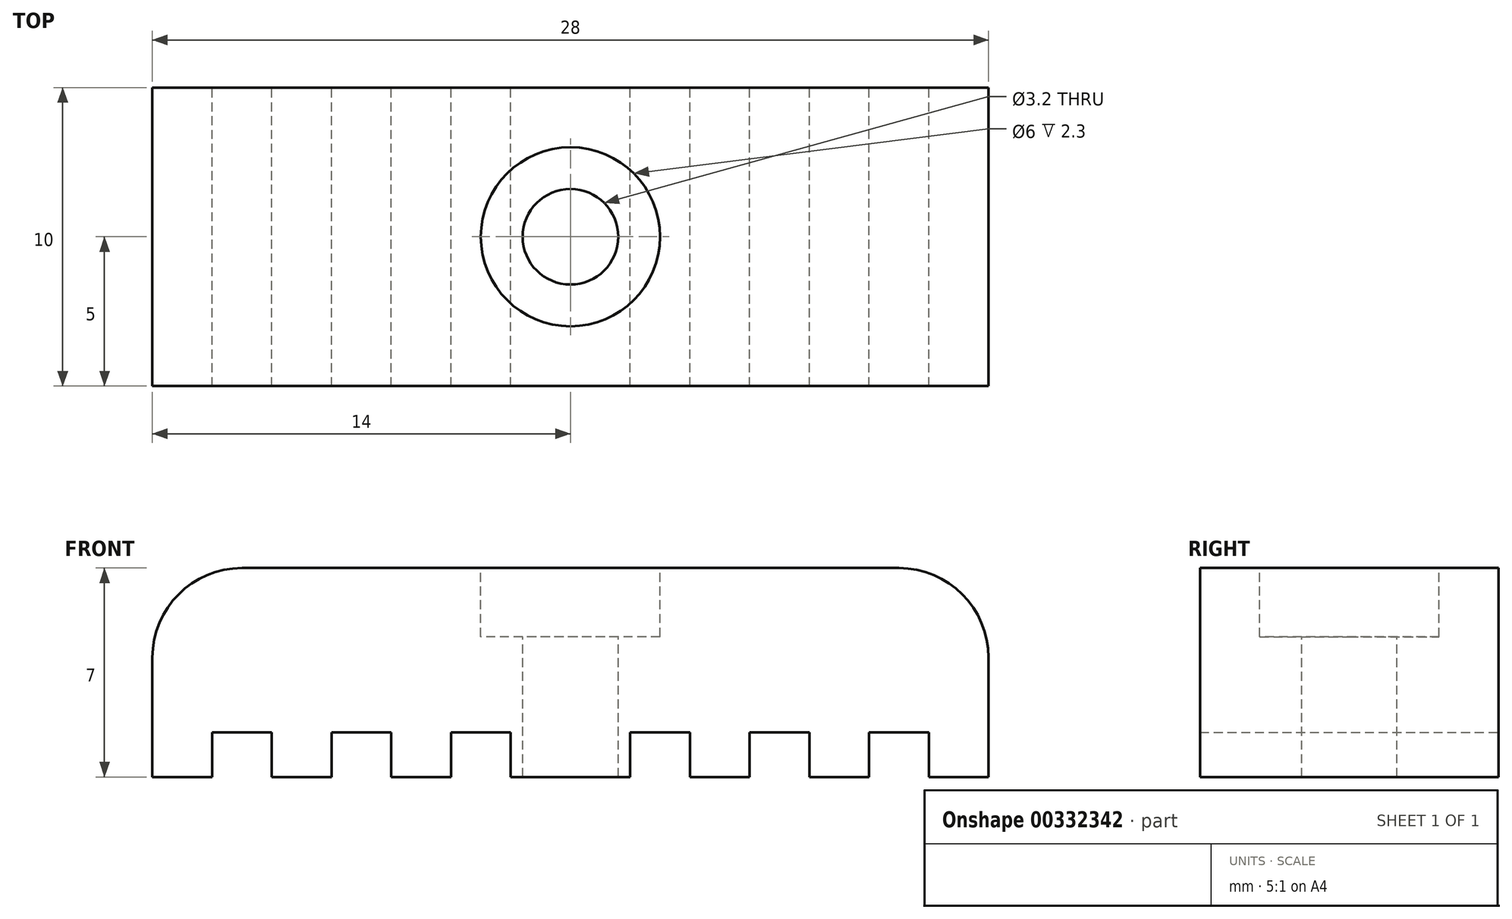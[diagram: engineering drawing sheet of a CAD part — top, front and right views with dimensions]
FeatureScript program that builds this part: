
annotation { "Feature Type Name" : "Feature", "Feature Type Description" : "" }
export const myFeature = defineFeature(function(context is Context, id is Id, definition is map)
    precondition{}
    {
        {
            var Q0;
            Q0=qCreatedBy(makeId("Front.planeOp"),FACE);
            var sketch = newSketch(context, id + "F0", { "sketchPlane" : qUnion([Q0])});
            skLineSegment(sketch, "E0.bottom", {"start": v(14, -3.5) * mm, "end": v(-14, -3.5) * mm});
            skLineSegment(sketch, "E0.top", {"start": v(14, 3.5) * mm, "end": v(-14, 3.5) * mm});
            skLineSegment(sketch, "E0.left", {"start": v(14, -3.5) * mm, "end": v(14, 3.5) * mm});
            skLineSegment(sketch, "E0.right", {"start": v(-14, -3.5) * mm, "end": v(-14, 3.5) * mm});
            skPoint(sketch, "E0.middle", {"position": v(0, 0) * mm});
            skLineSegment(sketch, "E1", {"start": v(-4, -2) * mm, "end": v(-4, -3.5) * mm});
            skLineSegment(sketch, "E2", {"start": v(-4, -3.5) * mm, "end": v(-6, -3.5) * mm});
            skLineSegment(sketch, "E3", {"start": v(-6, -3.5) * mm, "end": v(-6, -2) * mm});
            skLineSegment(sketch, "E4", {"start": v(-6, -2) * mm, "end": v(-8, -2) * mm});
            skLineSegment(sketch, "E5", {"start": v(-8, -2) * mm, "end": v(-8, -3.5) * mm});
            skLineSegment(sketch, "E6", {"start": v(-8, -3.5) * mm, "end": v(-10, -3.5) * mm});
            skLineSegment(sketch, "E7", {"start": v(-10, -3.5) * mm, "end": v(-10, -2) * mm});
            skLineSegment(sketch, "E8", {"start": v(-10, -2) * mm, "end": v(-12, -2) * mm});
            skLineSegment(sketch, "E9", {"start": v(-12, -2) * mm, "end": v(-12, -3.5) * mm});
            skLineSegment(sketch, "E10", {"start": v(-4, -2) * mm, "end": v(-2, -2) * mm});
            skLineSegment(sketch, "E11", {"start": v(-2, -2) * mm, "end": v(-2, -3.5) * mm});
            skLineSegment(sketch, "E12.MirrorCS", {"start": v(2, -2) * mm, "end": v(2, -3.5) * mm});
            skLineSegment(sketch, "E13.MirrorCS", {"start": v(4, -2) * mm, "end": v(2, -2) * mm});
            skLineSegment(sketch, "E14.MirrorCS", {"start": v(4, -2) * mm, "end": v(4, -3.5) * mm});
            skLineSegment(sketch, "E15.MirrorCS", {"start": v(6, -3.5) * mm, "end": v(6, -2) * mm});
            skLineSegment(sketch, "E16.MirrorCS", {"start": v(6, -2) * mm, "end": v(8, -2) * mm});
            skLineSegment(sketch, "E17.MirrorCS", {"start": v(8, -2) * mm, "end": v(8, -3.5) * mm});
            skLineSegment(sketch, "E18.MirrorCS", {"start": v(10, -3.5) * mm, "end": v(10, -2) * mm});
            skLineSegment(sketch, "E19.MirrorCS", {"start": v(10, -2) * mm, "end": v(12, -2) * mm});
            skLineSegment(sketch, "E20.MirrorCS", {"start": v(12, -2) * mm, "end": v(12, -3.5) * mm});
            skSolve(sketch);
        }
        {
            var Q0;
            Q0=makeQuery(id+"F0.imprint","IMPRINT",FACE,{"disambiguationData":[TD([[makeQuery(id+"F0.imprint","IMPRINT",EDGE,{"derivedFrom":sQuery(id+"F0.wireOp",EDGE,"E0.top")}),1.0]])]});
            extrude(context, id + "F1", {"entities" : qUnion([Q0]), "depth" : 10 * mm, "offsetDistance" : 25 * mm});
        }
        {
            var Q0;
            Q0=makeQuery(id+"F1.opExtrude","SWEPT_FACE",FACE,{"disambiguationData":[OSD([sQuery(id+"F0.wireOp",EDGE,"E0.top")])]});
            var sketch = newSketch(context, id + "F2", { "sketchPlane" : qUnion([Q0])});
            skCircle(sketch, "E21", {"center": v(0, -5) * mm, "radius": 3 * mm});
            skCircle(sketch, "E22", {"center": v(0, -5) * mm, "radius": 1.6 * mm});
            skSolve(sketch);
        }
        {
            var Q0;
            Q0=makeQuery(id+"F2.imprint","IMPRINT",FACE,{"disambiguationData":[TD([[makeQuery(id+"F2.imprint","IMPRINT",EDGE,{"derivedFrom":sQuery(id+"F2.wireOp",EDGE,"E22")}),1.0]])]});
            extrude(context, id + "F3", {"entities" : qUnion([Q0]), "operationType" : NewBodyOperationType.REMOVE, "oppositeDirection" : true, "depth" : 25 * mm, "offsetDistance" : 25 * mm});
        }
        {
            var Q0;
            Q0=makeQuery(id+"F2.imprint","IMPRINT",FACE,{"disambiguationData":[TD([[makeQuery(id+"F2.imprint","IMPRINT",EDGE,{"derivedFrom":sQuery(id+"F2.wireOp",EDGE,"E21")}),1.0]])]});
            extrude(context, id + "F4", {"entities" : qUnion([Q0]), "operationType" : NewBodyOperationType.REMOVE, "oppositeDirection" : true, "depth" : 2.3 * mm, "offsetDistance" : 25 * mm});
        }
        {
            var Q0;
            Q0=makeQuery(id+"F1.opExtrude","SWEPT_EDGE",EDGE,{"disambiguationData":[OSD([sQuery(id+"F0.wireOp",EDGE,"E0.top"),sQuery(id+"F0.wireOp",EDGE,"E0.right")])]});
            var Q1;
            Q1=makeQuery(id+"F1.opExtrude","SWEPT_EDGE",EDGE,{"disambiguationData":[OSD([sQuery(id+"F0.wireOp",EDGE,"E0.top"),sQuery(id+"F0.wireOp",EDGE,"E0.left")])]});
            fillet(context, id + "F5", {"entities" : qUnion([Q0, Q1]), "tangentPropagation" : true, "radius" : 3 * mm, "defaultsChanged" : true, "vertexSettings" : [], "allowEdgeOverflow" : false});
        }
    });
